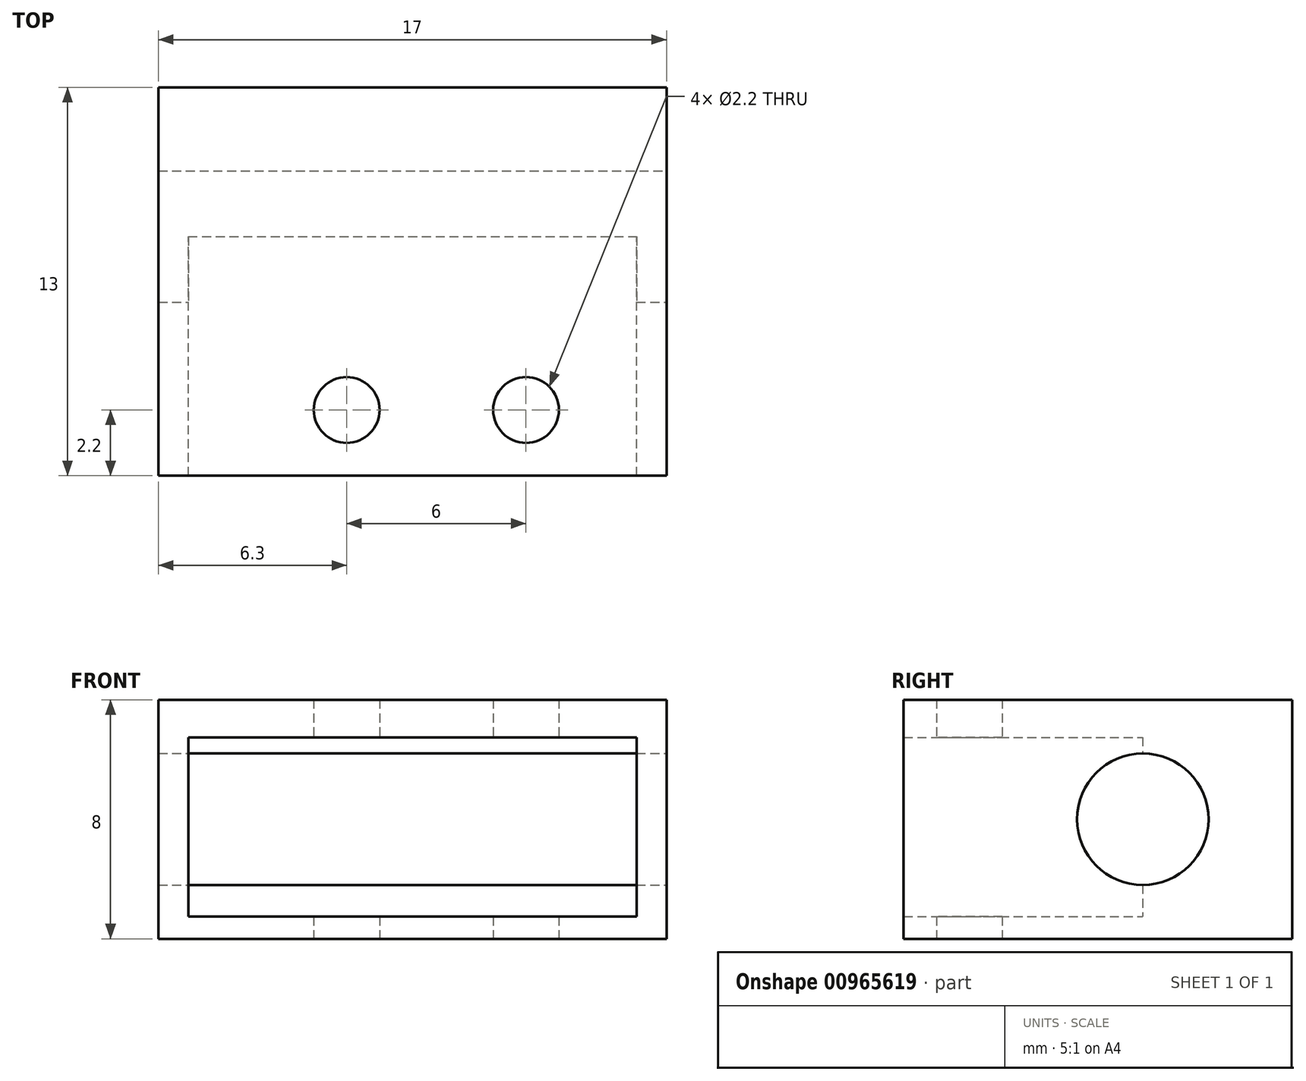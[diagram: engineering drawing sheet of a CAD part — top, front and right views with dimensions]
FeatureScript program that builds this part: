
annotation { "Feature Type Name" : "Feature", "Feature Type Description" : "" }
export const myFeature = defineFeature(function(context is Context, id is Id, definition is map)
    precondition{}
    {
        {
            var Q0;
            Q0=qCreatedBy(makeId("Top.planeOp"),FACE);
            var sketch = newSketch(context, id + "F0", { "sketchPlane" : qUnion([Q0])});
            skPoint(sketch, "E0.middle", {"position": v(0, 0) * mm});
            skCircle(sketch, "E1", {"center": v(-3, -2.3) * mm, "radius": 1.1 * mm});
            skCircle(sketch, "E2", {"center": v(3, -2.3) * mm, "radius": 1.1 * mm});
            skLineSegment(sketch, "E3.bottom", {"start": v(-6.35, 3.5) * mm, "end": v(6.35, 3.5) * mm});
            skLineSegment(sketch, "E3.top", {"start": v(-6.35, -3.5) * mm, "end": v(6.35, -3.5) * mm});
            skLineSegment(sketch, "E3.left", {"start": v(-6.35, 3.5) * mm, "end": v(-6.35, -3.5) * mm});
            skLineSegment(sketch, "E3.right", {"start": v(6.35, 3.5) * mm, "end": v(6.35, -3.5) * mm});
            skLineSegment(sketch, "E4.bottom", {"start": v(7.7, -4.5) * mm, "end": v(-9.3, -4.5) * mm});
            skLineSegment(sketch, "E4.top", {"start": v(7.7, 8.5) * mm, "end": v(-9.3, 8.5) * mm});
            skLineSegment(sketch, "E4.left", {"start": v(7.7, -4.5) * mm, "end": v(7.7, 8.5) * mm});
            skLineSegment(sketch, "E4.right", {"start": v(-9.3, -4.5) * mm, "end": v(-9.3, 8.5) * mm});
            skSolve(sketch);
        }
        {
            var Q0;
            Q0=makeQuery(id+"F0.imprint","IMPRINT",FACE,{"disambiguationData":[TD([[makeQuery(id+"F0.imprint","IMPRINT",EDGE,{"derivedFrom":sQuery(id+"F0.wireOp",EDGE,"E1")}),-1.0]])]});
            var Q1;
            Q1=makeQuery(id+"F0.imprint","IMPRINT",FACE,{"disambiguationData":[TD([[makeQuery(id+"F0.imprint","IMPRINT",EDGE,{"derivedFrom":sQuery(id+"F0.wireOp",EDGE,"E3.bottom")}),1.0]])]});
            extrude(context, id + "F1", {"entities" : qUnion([Q0, Q1]), "depth" : 8 * mm, "offsetDistance" : 25 * mm});
        }
        {
            var Q0;
            Q0=qCreatedBy(makeId("Front.planeOp"),FACE);
            var sketch = newSketch(context, id + "F2", { "sketchPlane" : qUnion([Q0])});
            skLineSegment(sketch, "E5.bottom", {"start": v(-8.3, 6.75) * mm, "end": v(6.7, 6.75) * mm});
            skLineSegment(sketch, "E5.top", {"start": v(-8.3, 0.75) * mm, "end": v(6.7, 0.75) * mm});
            skLineSegment(sketch, "E5.left", {"start": v(-8.3, 6.75) * mm, "end": v(-8.3, 0.75) * mm});
            skLineSegment(sketch, "E5.right", {"start": v(6.7, 6.75) * mm, "end": v(6.7, 0.75) * mm});
            skSolve(sketch);
        }
        {
            var Q0;
            Q0=makeQuery(id+"F2.imprint","IMPRINT",FACE,{"disambiguationData":[TD([[makeQuery(id+"F2.imprint","IMPRINT",EDGE,{"derivedFrom":sQuery(id+"F2.wireOp",EDGE,"E5.bottom")}),-1.0]])]});
            extrude(context, id + "F3", {"entities" : qUnion([Q0]), "operationType" : NewBodyOperationType.REMOVE, "endBound" : BoundingType.THROUGH_ALL, "depth" : 25 * mm, "offsetDistance" : 25 * mm, "hasSecondDirection" : true, "secondDirectionOppositeDirection" : true, "secondDirectionDepth" : 3.5 * mm});
        }
        {
            var Q0;
            Q0=qCreatedBy(makeId("Right.planeOp"),FACE);
            var sketch = newSketch(context, id + "F4", { "sketchPlane" : qUnion([Q0])});
            skCircle(sketch, "E6", {"center": v(3.5, 4) * mm, "radius": 2.2 * mm});
            skSolve(sketch);
        }
        {
            var Q0;
            Q0=makeQuery(id+"F4.imprint","IMPRINT",FACE,{"disambiguationData":[TD([[makeQuery(id+"F4.imprint","IMPRINT",EDGE,{"derivedFrom":sQuery(id+"F4.wireOp",EDGE,"E6")}),1.0]])]});
            extrude(context, id + "F5", {"entities" : qUnion([Q0]), "operationType" : NewBodyOperationType.REMOVE, "endBound" : BoundingType.THROUGH_ALL, "oppositeDirection" : true, "depth" : 25 * mm, "offsetDistance" : 25 * mm, "hasSecondDirection" : true, "secondDirectionBound" : SecondDirectionBoundingType.THROUGH_ALL, "secondDirectionOppositeDirection" : false, "secondDirectionDepth" : 25 * mm});
        }
    });
